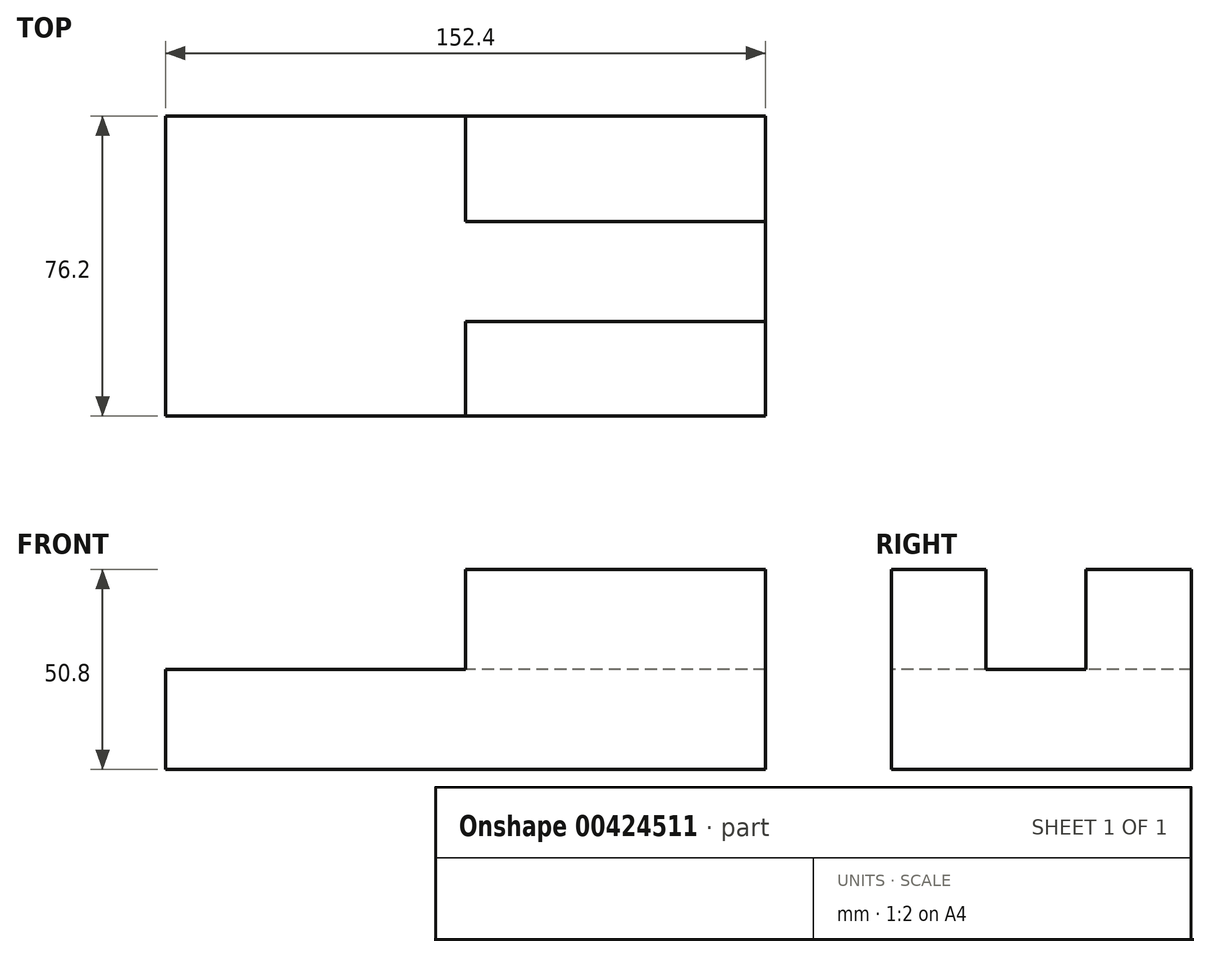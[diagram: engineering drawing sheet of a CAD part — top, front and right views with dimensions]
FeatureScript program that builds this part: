
annotation { "Feature Type Name" : "Feature", "Feature Type Description" : "" }
export const myFeature = defineFeature(function(context is Context, id is Id, definition is map)
    precondition{}
    {
        {
            var Q0;
            Q0=qCreatedBy(makeId("Front.planeOp"),FACE);
            var sketch = newSketch(context, id + "F0", { "sketchPlane" : qUnion([Q0])});
            skLineSegment(sketch, "E0", {"start": v(0, 0) * mm, "end": v(0, 50.8) * mm});
            skLineSegment(sketch, "E1", {"start": v(0, 50.8) * mm, "end": v(152.4, 50.8) * mm});
            skLineSegment(sketch, "E2", {"start": v(152.4, 50.8) * mm, "end": v(152.4, 0) * mm});
            skLineSegment(sketch, "E3", {"start": v(152.4, 0) * mm, "end": v(0, 0) * mm});
            skSolve(sketch);
        }
        {
            var Q0;
            Q0=makeQuery(id+"F0.imprint","IMPRINT",FACE,{"disambiguationData":[TD([[makeQuery(id+"F0.imprint","IMPRINT",EDGE,{"derivedFrom":sQuery(id+"F0.wireOp",EDGE,"E0")}),-1.0]])]});
            extrude(context, id + "F1", {"entities" : qUnion([Q0]), "depth" : 76.2 * mm});
        }
        {
            var Q0;
            Q0=makeQuery(id+"F1.opExtrude","SWEPT_FACE",FACE,{"disambiguationData":[OSD([sQuery(id+"F0.wireOp",EDGE,"E1")])]});
            var sketch = newSketch(context, id + "F2", { "sketchPlane" : qUnion([Q0])});
            skLineSegment(sketch, "E4", {"start": v(152.4, -26.83) * mm, "end": v(76.2, -26.83) * mm});
            skLineSegment(sketch, "E5", {"start": v(76.2, -26.83) * mm, "end": v(76.2, -52.23) * mm});
            skLineSegment(sketch, "E6", {"start": v(76.2, -52.23) * mm, "end": v(152.4, -52.23) * mm});
            skLineSegment(sketch, "E7", {"start": v(152.4, -52.23) * mm, "end": v(152.4, -26.83) * mm});
            skSolve(sketch);
        }
        {
            var Q0;
            Q0=makeQuery(id+"F2.imprint","IMPRINT",FACE,{"disambiguationData":[TD([[makeQuery(id+"F2.imprint","IMPRINT",EDGE,{"derivedFrom":sQuery(id+"F2.wireOp",EDGE,"E4")}),1.0]])]});
            extrude(context, id + "F3", {"entities" : qUnion([Q0]), "operationType" : NewBodyOperationType.REMOVE, "oppositeDirection" : true, "depth" : 25.4 * mm});
        }
        {
            var Q0;
            Q0=makeQuery(id+"F1.opExtrude","SWEPT_FACE",FACE,{"disambiguationData":[OSD([sQuery(id+"F0.wireOp",EDGE,"E1")])]});
            var sketch = newSketch(context, id + "F4", { "sketchPlane" : qUnion([Q0])});
            skLineSegment(sketch, "E8", {"start": v(76.2, 0) * mm, "end": v(76.2, -76.2) * mm});
            skLineSegment(sketch, "E9", {"start": v(76.2, -76.2) * mm, "end": v(0, -76.2) * mm});
            skLineSegment(sketch, "E10", {"start": v(0, -76.2) * mm, "end": v(0, 0) * mm});
            skLineSegment(sketch, "E11", {"start": v(0, 0) * mm, "end": v(76.2, 0) * mm});
            skSolve(sketch);
        }
        {
            var Q0;
            {var subQ0=sQuery(id+"F4.wireOp",EDGE,"E9");Q0=makeQuery(id+"F4.imprint","IMPRINT",FACE,{"disambiguationData":[TD([[makeQuery(id+"F4.imprint","IMPRINT",EDGE,{"derivedFrom":subQ0}),1.0]])]});}
            extrude(context, id + "F5", {"entities" : qUnion([Q0]), "operationType" : NewBodyOperationType.REMOVE, "oppositeDirection" : true, "depth" : 25.4 * mm});
        }
    });
